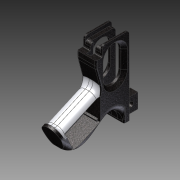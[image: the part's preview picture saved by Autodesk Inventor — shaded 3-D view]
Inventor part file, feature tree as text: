
AUTODESK INVENTOR PART (.ipt)
format: ipt  version: 2012 (Build 160160000, 160)  size: 534,528 bytes
history: native  units: mm
features: fillet x15, extrude x10, sketch x2, chamfer x1
ambient origin geometry x8: Origin, YZ Plane, XZ Plane, XY Plane, X Axis, Y Axis, Z Axis, Center Point
feature tree (28):
  sketch  "Sketch2"  dims[d14=52.0mm d15=23.0mm d16=22.6mm d17=8.2mm d18=11.5mm d19=11.5mm d20=10.2mm d21=10.2mm d22=8.0mm d23=20.0mm d25=30.0mm d26=0.0mm d27=11.8mm d28=0.0mm]
  extrude  "Extrusion3"  Depth=11.8mm TaperAngle=0.0deg
  extrude  "Extrusion4"  Depth=1.5mm
  fillet  "Fillet1"  Radius=4.18879mm
  fillet  "Fillet2"  Radius=4.0mm
  extrude  "Extrusion5"  Depth=30.0mm TaperAngle=0.0deg
  extrude  "Extrusion6"  Depth=24.0mm TaperAngle=0.0deg
  extrude  "Extrusion7"  Depth=28.0mm
  fillet  "Fillet3"  Radius=18.0mm
  fillet  "Fillet4"  Radius=28.0mm
  fillet  "Fillet5"  Radius=22.0mm
  fillet  "Fillet6"  Radius=24.0mm
  fillet  "Fillet7"  Radius=117.0mm
  chamfer  "Chamfer1"  Distance=54.0mm
  fillet  "Fillet8"  Radius=43.0mm
  fillet  "Fillet9"  Radius=12.0mm
  fillet  "Fillet10"  Radius=15.0mm
  fillet  "Fillet11"  Radius=10.0mm
  fillet  "Fillet12"  Radius=6.0mm
  extrude  "Extrusion8"  Depth=10.0mm
  fillet  "Fillet13"  Radius=5.0mm
  fillet  "Fillet14"  Radius=20.0mm
  sketch  "Sketch3"  dims[d29=4.5mm d30=1.5mm d37=4.18879mm d39=4.0mm d41=30.0mm d42=0.0mm d43=24.0mm d44=0.0mm d45=28.0mm d46=18.0mm d47=28.0mm d48=22.0mm d49=24.0mm d50=0.0mm d52=117.0mm d53=54.0mm d54=43.0mm d55=12.0mm d56=15.0mm d57=10.0mm d58=6.0mm d59=10.0mm d60=5.0mm d61=2.0mm d62=45.0deg d63=20.0mm d64=2.0mm d65=108.0mm d66=2.0mm d67=20.0mm d68=4.5mm d69=5.8mm d70=24.4mm d71=0.0mm d72=5.0mm d73=1.5mm d74=38.0mm d75=90.0mm d76=12.6mm d77=0.0mm d78=11.0mm d79=19.0mm d80=42.0mm d81=7.0mm d82=0.0mm d83=2.0mm d84=4.0mm d85=66.0mm d86=6.0mm d88=60.0mm d89=8.0mm d90=3.0mm d93=3.0mm d94=3.0mm d95=3.0mm d96=3.0mm d98=10.0mm d99=40.0mm d100=0.0mm d101=0.0mm d102=11.0mm d103=10.0mm d104=0.0mm d105=0.0mm d106=38.0mm d107=3.0mm d108=3.0mm d109=3.0mm d111=3.0mm d112=30.0mm d113=6.0mm d114=73.0mm]
  extrude  "Extrusion9"  Depth=2.0mm
  extrude  "Extrusion10"  Depth=108.0mm
  fillet  "Fillet15"  Radius=2.0mm
  extrude  "Extrusion11"  Depth=20.0mm
  extrude  "Extrusion12"  Depth=4.5mm
